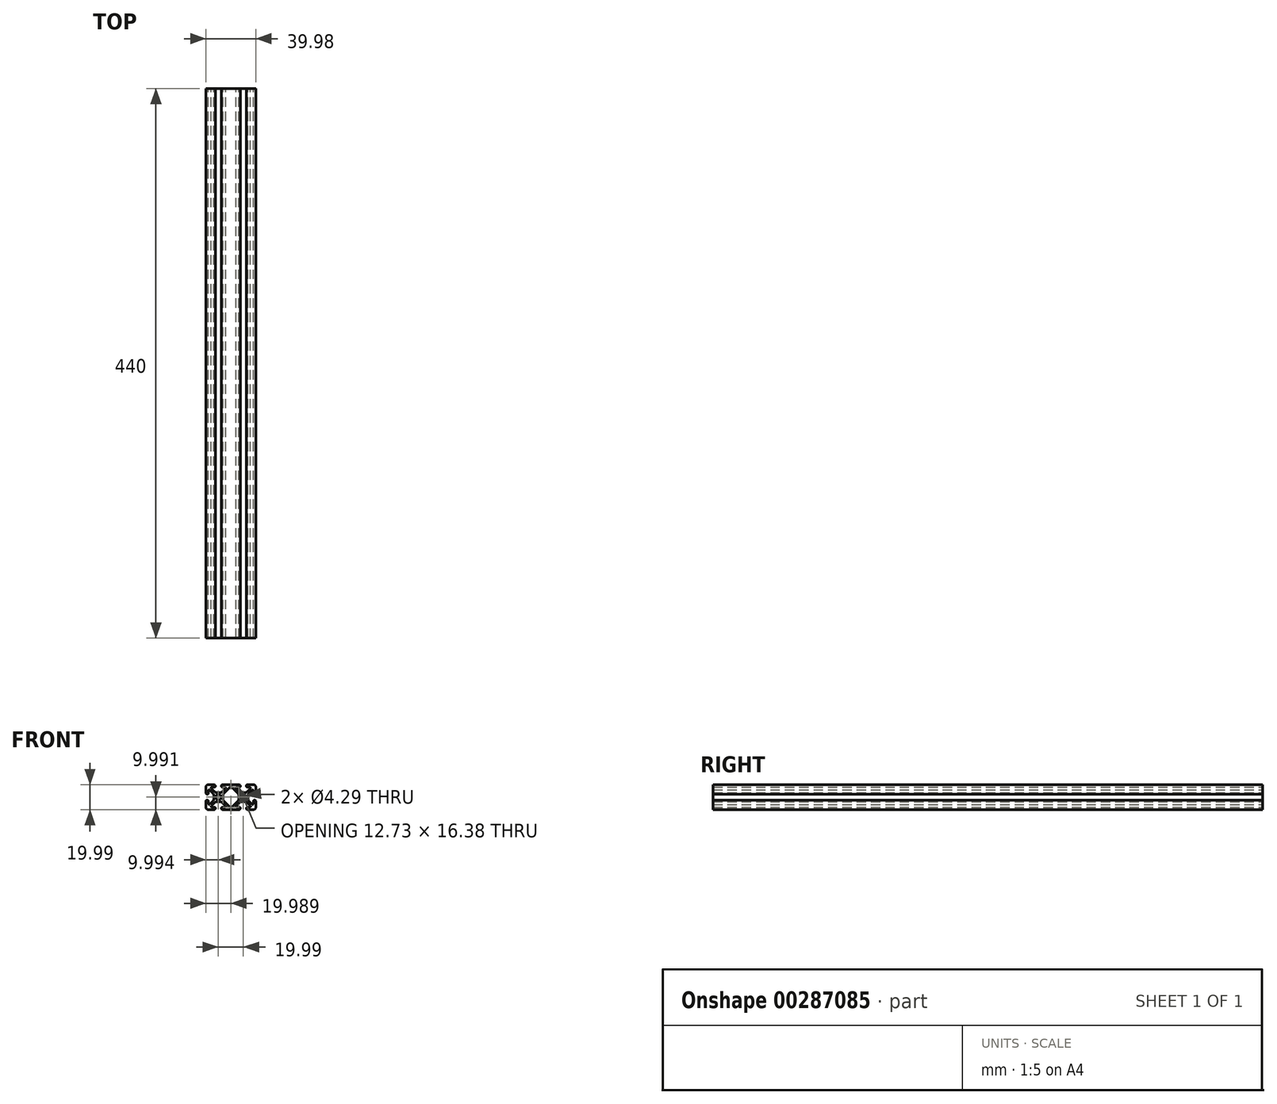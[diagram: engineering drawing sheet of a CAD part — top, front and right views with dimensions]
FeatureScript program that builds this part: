
annotation { "Feature Type Name" : "Feature", "Feature Type Description" : "" }
export const myFeature = defineFeature(function(context is Context, id is Id, definition is map)
    precondition{}
    {
        {
            var Q0;
            Q0=qCreatedBy(makeId("Front.planeOp"),FACE);
            var sketch = newSketch(context, id + "F0", { "sketchPlane" : qUnion([Q0])});
            skArc(sketch, "E0.0.0", {"start": v(-12.02, 4.76) * mm, "mid": v(-13.17, 4.99) * mm, "end": v(-14.14, 5.64) * mm});
            skLineSegment(sketch, "E0.0.1", {"start": v(-14.14, 5.64) * mm, "end": v(-16.4, 7.9) * mm});
            skArc(sketch, "E0.0.2", {"start": v(-16.4, 7.9) * mm, "mid": v(-16.58, 8.8) * mm, "end": v(-15.8, 9.32) * mm});
            skLineSegment(sketch, "E0.0.3", {"start": v(-15.8, 9.32) * mm, "end": v(-13.7, 9.32) * mm});
            skArc(sketch, "E0.0.4", {"start": v(-13.7, 9.32) * mm, "mid": v(-13.48, 9.41) * mm, "end": v(-13.39, 9.63) * mm});
            skLineSegment(sketch, "E0.0.5", {"start": v(-13.39, 9.63) * mm, "end": v(-13.39, 10.34) * mm});
            skArc(sketch, "E0.0.6", {"start": v(-13.39, 10.34) * mm, "mid": v(-13.62, 10.9) * mm, "end": v(-14.18, 11.13) * mm});
            skLineSegment(sketch, "E0.0.7", {"start": v(-14.18, 11.13) * mm, "end": v(-18.87, 11.13) * mm});
            skArc(sketch, "E0.0.8", {"start": v(-18.87, 11.13) * mm, "mid": v(-20.3, 10.54) * mm, "end": v(-20.88, 9.12) * mm});
            skLineSegment(sketch, "E0.0.9", {"start": v(-20.88, 9.12) * mm, "end": v(-20.88, 4.42) * mm});
            skArc(sketch, "E0.0.10", {"start": v(-20.88, 4.42) * mm, "mid": v(-20.65, 3.86) * mm, "end": v(-20.1, 3.63) * mm});
            skLineSegment(sketch, "E0.0.11", {"start": v(-20.1, 3.63) * mm, "end": v(-19.38, 3.63) * mm});
            skArc(sketch, "E0.0.12", {"start": v(-19.38, 3.63) * mm, "mid": v(-19.17, 3.72) * mm, "end": v(-19.08, 3.94) * mm});
            skLineSegment(sketch, "E0.0.13", {"start": v(-19.08, 3.94) * mm, "end": v(-19.08, 6.05) * mm});
            skArc(sketch, "E0.0.14", {"start": v(-19.08, 6.05) * mm, "mid": v(-18.56, 6.82) * mm, "end": v(-17.65, 6.64) * mm});
            skLineSegment(sketch, "E0.0.15", {"start": v(-17.65, 6.64) * mm, "end": v(-15.4, 4.38) * mm});
            skArc(sketch, "E0.0.16", {"start": v(-15.4, 4.38) * mm, "mid": v(-14.74, 3.41) * mm, "end": v(-14.51, 2.26) * mm});
            skLineSegment(sketch, "E0.0.17", {"start": v(-14.51, 2.26) * mm, "end": v(-14.51, 0) * mm});
            skArc(sketch, "E0.0.18", {"start": v(-14.51, 0) * mm, "mid": v(-14.74, -1.15) * mm, "end": v(-15.4, -2.12) * mm});
            skLineSegment(sketch, "E0.0.19", {"start": v(-15.4, -2.12) * mm, "end": v(-17.65, -4.38) * mm});
            skArc(sketch, "E0.0.20", {"start": v(-17.65, -4.38) * mm, "mid": v(-18.56, -4.56) * mm, "end": v(-19.08, -3.78) * mm});
            skLineSegment(sketch, "E0.0.21", {"start": v(-19.08, -3.78) * mm, "end": v(-19.08, -1.68) * mm});
            skArc(sketch, "E0.0.22", {"start": v(-19.08, -1.68) * mm, "mid": v(-19.17, -1.46) * mm, "end": v(-19.38, -1.37) * mm});
            skLineSegment(sketch, "E0.0.23", {"start": v(-19.38, -1.37) * mm, "end": v(-20.1, -1.37) * mm});
            skArc(sketch, "E0.0.24", {"start": v(-20.1, -1.37) * mm, "mid": v(-20.65, -1.6) * mm, "end": v(-20.88, -2.16) * mm});
            skLineSegment(sketch, "E0.0.25", {"start": v(-20.88, -2.16) * mm, "end": v(-20.88, -6.86) * mm});
            skArc(sketch, "E0.0.26", {"start": v(-20.88, -6.86) * mm, "mid": v(-20.3, -8.28) * mm, "end": v(-18.87, -8.86) * mm});
            skLineSegment(sketch, "E0.0.27", {"start": v(-18.87, -8.86) * mm, "end": v(-14.18, -8.86) * mm});
            skArc(sketch, "E0.0.28", {"start": v(-14.18, -8.86) * mm, "mid": v(-13.62, -8.63) * mm, "end": v(-13.39, -8.08) * mm});
            skLineSegment(sketch, "E0.0.29", {"start": v(-13.39, -8.08) * mm, "end": v(-13.39, -7.36) * mm});
            skArc(sketch, "E0.0.30", {"start": v(-13.39, -7.36) * mm, "mid": v(-13.48, -7.15) * mm, "end": v(-13.7, -7.06) * mm});
            skLineSegment(sketch, "E0.0.31", {"start": v(-13.7, -7.06) * mm, "end": v(-15.8, -7.06) * mm});
            skArc(sketch, "E0.0.32", {"start": v(-15.8, -7.06) * mm, "mid": v(-16.58, -6.54) * mm, "end": v(-16.4, -5.63) * mm});
            skLineSegment(sketch, "E0.0.33", {"start": v(-16.4, -5.63) * mm, "end": v(-14.14, -3.37) * mm});
            skArc(sketch, "E0.0.34", {"start": v(-14.14, -3.37) * mm, "mid": v(-13.17, -2.72) * mm, "end": v(-12.02, -2.5) * mm});
            skLineSegment(sketch, "E0.0.35", {"start": v(-12.02, -2.5) * mm, "end": v(-9.75, -2.5) * mm});
            skArc(sketch, "E0.0.36", {"start": v(-9.75, -2.5) * mm, "mid": v(-8.6, -2.72) * mm, "end": v(-7.63, -3.37) * mm});
            skLineSegment(sketch, "E0.0.37", {"start": v(-7.63, -3.37) * mm, "end": v(-5.38, -5.63) * mm});
            skArc(sketch, "E0.0.38", {"start": v(-5.38, -5.63) * mm, "mid": v(-5.2, -6.54) * mm, "end": v(-5.97, -7.06) * mm});
            skLineSegment(sketch, "E0.0.39", {"start": v(-5.97, -7.06) * mm, "end": v(-8.08, -7.06) * mm});
            skArc(sketch, "E0.0.40", {"start": v(-8.08, -7.06) * mm, "mid": v(-8.3, -7.15) * mm, "end": v(-8.38, -7.36) * mm});
            skLineSegment(sketch, "E0.0.41", {"start": v(-8.38, -7.36) * mm, "end": v(-8.38, -8.08) * mm});
            skArc(sketch, "E0.0.42", {"start": v(-8.38, -8.08) * mm, "mid": v(-8.15, -8.63) * mm, "end": v(-7.6, -8.86) * mm});
            skLineSegment(sketch, "E0.0.43", {"start": v(-7.6, -8.86) * mm, "end": v(5.81, -8.86) * mm});
            skArc(sketch, "E0.0.44", {"start": v(5.81, -8.86) * mm, "mid": v(6.37, -8.63) * mm, "end": v(6.6, -8.08) * mm});
            skLineSegment(sketch, "E0.0.45", {"start": v(6.6, -8.08) * mm, "end": v(6.6, -7.36) * mm});
            skArc(sketch, "E0.0.46", {"start": v(6.6, -7.36) * mm, "mid": v(6.51, -7.15) * mm, "end": v(6.3, -7.06) * mm});
            skLineSegment(sketch, "E0.0.47", {"start": v(6.3, -7.06) * mm, "end": v(4.19, -7.06) * mm});
            skArc(sketch, "E0.0.48", {"start": v(4.19, -7.06) * mm, "mid": v(3.41, -6.54) * mm, "end": v(3.6, -5.63) * mm});
            skLineSegment(sketch, "E0.0.49", {"start": v(3.6, -5.63) * mm, "end": v(5.85, -3.37) * mm});
            skArc(sketch, "E0.0.50", {"start": v(5.85, -3.37) * mm, "mid": v(6.82, -2.72) * mm, "end": v(7.97, -2.5) * mm});
            skLineSegment(sketch, "E0.0.51", {"start": v(7.97, -2.5) * mm, "end": v(10.24, -2.5) * mm});
            skArc(sketch, "E0.0.52", {"start": v(10.24, -2.5) * mm, "mid": v(11.38, -2.72) * mm, "end": v(12.36, -3.37) * mm});
            skLineSegment(sketch, "E0.0.53", {"start": v(12.36, -3.37) * mm, "end": v(14.61, -5.63) * mm});
            skArc(sketch, "E0.0.54", {"start": v(14.61, -5.63) * mm, "mid": v(14.8, -6.54) * mm, "end": v(14.02, -7.06) * mm});
            skLineSegment(sketch, "E0.0.55", {"start": v(14.02, -7.06) * mm, "end": v(11.91, -7.06) * mm});
            skArc(sketch, "E0.0.56", {"start": v(11.91, -7.06) * mm, "mid": v(11.7, -7.15) * mm, "end": v(11.6, -7.36) * mm});
            skLineSegment(sketch, "E0.0.57", {"start": v(11.6, -7.36) * mm, "end": v(11.6, -8.08) * mm});
            skArc(sketch, "E0.0.58", {"start": v(11.6, -8.08) * mm, "mid": v(11.84, -8.63) * mm, "end": v(12.4, -8.86) * mm});
            skLineSegment(sketch, "E0.0.59", {"start": v(12.4, -8.86) * mm, "end": v(17.1, -8.86) * mm});
            skArc(sketch, "E0.0.60", {"start": v(17.1, -8.86) * mm, "mid": v(18.51, -8.28) * mm, "end": v(19.1, -6.86) * mm});
            skLineSegment(sketch, "E0.0.61", {"start": v(19.1, -6.86) * mm, "end": v(19.1, -2.16) * mm});
            skArc(sketch, "E0.0.62", {"start": v(19.1, -2.16) * mm, "mid": v(18.87, -1.6) * mm, "end": v(18.31, -1.37) * mm});
            skLineSegment(sketch, "E0.0.63", {"start": v(18.31, -1.37) * mm, "end": v(17.6, -1.37) * mm});
            skArc(sketch, "E0.0.64", {"start": v(17.6, -1.37) * mm, "mid": v(17.38, -1.46) * mm, "end": v(17.3, -1.68) * mm});
            skLineSegment(sketch, "E0.0.65", {"start": v(17.3, -1.68) * mm, "end": v(17.3, -3.78) * mm});
            skArc(sketch, "E0.0.66", {"start": v(17.3, -3.78) * mm, "mid": v(16.78, -4.56) * mm, "end": v(15.86, -4.38) * mm});
            skLineSegment(sketch, "E0.0.67", {"start": v(15.86, -4.38) * mm, "end": v(13.6, -2.12) * mm});
            skArc(sketch, "E0.0.68", {"start": v(13.6, -2.12) * mm, "mid": v(12.96, -1.15) * mm, "end": v(12.73, 0) * mm});
            skLineSegment(sketch, "E0.0.69", {"start": v(12.73, 0) * mm, "end": v(12.73, 2.26) * mm});
            skArc(sketch, "E0.0.70", {"start": v(12.73, 2.26) * mm, "mid": v(12.96, 3.41) * mm, "end": v(13.6, 4.38) * mm});
            skLineSegment(sketch, "E0.0.71", {"start": v(13.6, 4.38) * mm, "end": v(15.86, 6.64) * mm});
            skArc(sketch, "E0.0.72", {"start": v(15.86, 6.64) * mm, "mid": v(16.78, 6.82) * mm, "end": v(17.3, 6.05) * mm});
            skLineSegment(sketch, "E0.0.73", {"start": v(17.3, 6.05) * mm, "end": v(17.3, 3.94) * mm});
            skArc(sketch, "E0.0.74", {"start": v(17.3, 3.94) * mm, "mid": v(17.38, 3.72) * mm, "end": v(17.6, 3.63) * mm});
            skLineSegment(sketch, "E0.0.75", {"start": v(17.6, 3.63) * mm, "end": v(18.31, 3.63) * mm});
            skArc(sketch, "E0.0.76", {"start": v(18.31, 3.63) * mm, "mid": v(18.87, 3.86) * mm, "end": v(19.1, 4.42) * mm});
            skLineSegment(sketch, "E0.0.77", {"start": v(19.1, 4.42) * mm, "end": v(19.1, 9.12) * mm});
            skArc(sketch, "E0.0.78", {"start": v(19.1, 9.12) * mm, "mid": v(18.51, 10.54) * mm, "end": v(17.1, 11.13) * mm});
            skLineSegment(sketch, "E0.0.79", {"start": v(17.1, 11.13) * mm, "end": v(12.4, 11.13) * mm});
            skArc(sketch, "E0.0.80", {"start": v(12.4, 11.13) * mm, "mid": v(11.84, 10.9) * mm, "end": v(11.6, 10.34) * mm});
            skLineSegment(sketch, "E0.0.81", {"start": v(11.6, 10.34) * mm, "end": v(11.6, 9.63) * mm});
            skArc(sketch, "E0.0.82", {"start": v(11.6, 9.63) * mm, "mid": v(11.7, 9.41) * mm, "end": v(11.91, 9.32) * mm});
            skLineSegment(sketch, "E0.0.83", {"start": v(11.91, 9.32) * mm, "end": v(14.02, 9.32) * mm});
            skArc(sketch, "E0.0.84", {"start": v(14.02, 9.32) * mm, "mid": v(14.8, 8.8) * mm, "end": v(14.61, 7.9) * mm});
            skLineSegment(sketch, "E0.0.85", {"start": v(14.61, 7.9) * mm, "end": v(12.36, 5.64) * mm});
            skArc(sketch, "E0.0.86", {"start": v(12.36, 5.64) * mm, "mid": v(11.38, 4.99) * mm, "end": v(10.24, 4.76) * mm});
            skLineSegment(sketch, "E0.0.87", {"start": v(10.24, 4.76) * mm, "end": v(7.97, 4.76) * mm});
            skArc(sketch, "E0.0.88", {"start": v(7.97, 4.76) * mm, "mid": v(6.82, 4.99) * mm, "end": v(5.85, 5.64) * mm});
            skLineSegment(sketch, "E0.0.89", {"start": v(5.85, 5.64) * mm, "end": v(3.6, 7.9) * mm});
            skArc(sketch, "E0.0.90", {"start": v(3.6, 7.9) * mm, "mid": v(3.41, 8.8) * mm, "end": v(4.19, 9.32) * mm});
            skLineSegment(sketch, "E0.0.91", {"start": v(4.19, 9.32) * mm, "end": v(6.3, 9.32) * mm});
            skArc(sketch, "E0.0.92", {"start": v(6.3, 9.32) * mm, "mid": v(6.51, 9.41) * mm, "end": v(6.6, 9.63) * mm});
            skLineSegment(sketch, "E0.0.93", {"start": v(6.6, 9.63) * mm, "end": v(6.6, 10.34) * mm});
            skArc(sketch, "E0.0.94", {"start": v(6.6, 10.34) * mm, "mid": v(6.37, 10.9) * mm, "end": v(5.81, 11.13) * mm});
            skLineSegment(sketch, "E0.0.95", {"start": v(5.81, 11.13) * mm, "end": v(-7.6, 11.13) * mm});
            skArc(sketch, "E0.0.96", {"start": v(-7.6, 11.13) * mm, "mid": v(-8.15, 10.9) * mm, "end": v(-8.38, 10.34) * mm});
            skLineSegment(sketch, "E0.0.97", {"start": v(-8.38, 10.34) * mm, "end": v(-8.38, 9.63) * mm});
            skArc(sketch, "E0.0.98", {"start": v(-8.38, 9.63) * mm, "mid": v(-8.3, 9.41) * mm, "end": v(-8.08, 9.32) * mm});
            skLineSegment(sketch, "E0.0.99", {"start": v(-8.08, 9.32) * mm, "end": v(-5.97, 9.32) * mm});
            skArc(sketch, "E0.0.100", {"start": v(-5.97, 9.32) * mm, "mid": v(-5.2, 8.8) * mm, "end": v(-5.38, 7.9) * mm});
            skLineSegment(sketch, "E0.0.101", {"start": v(-5.38, 7.9) * mm, "end": v(-7.63, 5.64) * mm});
            skArc(sketch, "E0.0.102", {"start": v(-7.63, 5.64) * mm, "mid": v(-8.6, 4.99) * mm, "end": v(-9.75, 4.76) * mm});
            skLineSegment(sketch, "E0.0.103", {"start": v(-9.75, 4.76) * mm, "end": v(-12.02, 4.76) * mm});
            skCircle(sketch, "E1.0", {"center": v(-10.89, 1.13) * mm, "radius": 2.15 * mm});
            skCircle(sketch, "E2.0", {"center": v(9.1, 1.13) * mm, "radius": 2.15 * mm});
            skLineSegment(sketch, "E3.0", {"start": v(-7.26, 2.26) * mm, "end": v(-7.26, 0) * mm});
            skArc(sketch, "E3.1", {"start": v(-6.38, 4.38) * mm, "mid": v(-7.03, 3.41) * mm, "end": v(-7.26, 2.26) * mm});
            skLineSegment(sketch, "E3.2", {"start": v(-1.83, 8.93) * mm, "end": v(-6.38, 4.38) * mm});
            skArc(sketch, "E3.3", {"start": v(-7.26, 0) * mm, "mid": v(-7.03, -1.15) * mm, "end": v(-6.38, -2.12) * mm});
            skLineSegment(sketch, "E3.4", {"start": v(-6.38, -2.12) * mm, "end": v(-1.83, -6.67) * mm});
            skArc(sketch, "E3.5", {"start": v(-1.83, -6.67) * mm, "mid": v(-0.9, -7.06) * mm, "end": v(0.05, -6.67) * mm});
            skLineSegment(sketch, "E3.6", {"start": v(0.05, -6.67) * mm, "end": v(4.6, -2.12) * mm});
            skLineSegment(sketch, "E3.7", {"start": v(4.6, 4.38) * mm, "end": v(0.05, 8.93) * mm});
            skLineSegment(sketch, "E3.8", {"start": v(5.48, 0) * mm, "end": v(5.48, 2.26) * mm});
            skArc(sketch, "E3.9", {"start": v(5.48, 2.26) * mm, "mid": v(5.25, 3.41) * mm, "end": v(4.6, 4.38) * mm});
            skArc(sketch, "E3.10", {"start": v(4.6, -2.12) * mm, "mid": v(5.25, -1.15) * mm, "end": v(5.48, 0) * mm});
            skArc(sketch, "E3.11", {"start": v(0.05, 8.93) * mm, "mid": v(-0.9, 9.32) * mm, "end": v(-1.83, 8.93) * mm});
            skSolve(sketch);
        }
        {
            var Q0;
            Q0=qSketchRegion(id+"F0",true);
            extrude(context, id + "F1", {"entities" : qUnion([Q0]), "depth" : 440 * mm});
        }
    });
